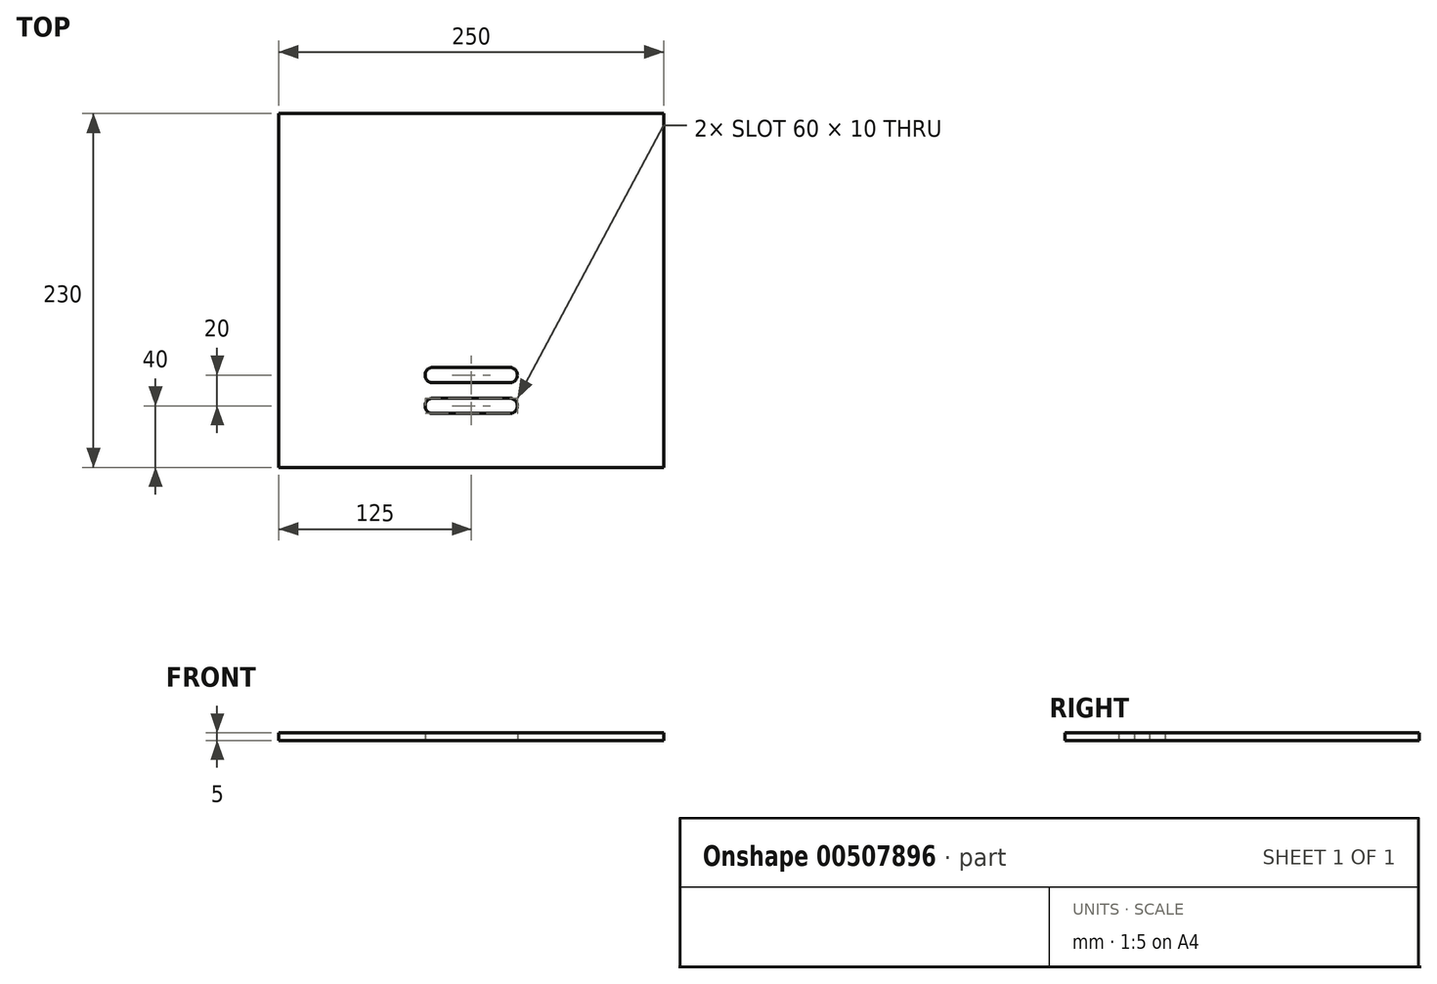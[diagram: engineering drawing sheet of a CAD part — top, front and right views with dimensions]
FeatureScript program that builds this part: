
annotation { "Feature Type Name" : "Feature", "Feature Type Description" : "" }
export const myFeature = defineFeature(function(context is Context, id is Id, definition is map)
    precondition{}
    {
        {
            var Q0;
            Q0=qCreatedBy(makeId("Top.planeOp"),FACE);
            var sketch = newSketch(context, id + "F0", { "sketchPlane" : qUnion([Q0])});
            skLineSegment(sketch, "E0.bottom", {"start": v(125, -115) * mm, "end": v(-125, -115) * mm});
            skLineSegment(sketch, "E0.top", {"start": v(125, 115) * mm, "end": v(-125, 115) * mm});
            skLineSegment(sketch, "E0.left", {"start": v(125, -115) * mm, "end": v(125, 115) * mm});
            skLineSegment(sketch, "E0.right", {"start": v(-125, -115) * mm, "end": v(-125, 115) * mm});
            skPoint(sketch, "E0.middle", {"position": v(0, 0) * mm});
            skLineSegment(sketch, "E1", {"start": v(0, -115) * mm, "end": v(0, 115) * mm, "construction": true});
            skLineSegment(sketch, "E2.1.0.0", {"start": v(25, -115) * mm, "end": v(25, 115) * mm, "construction": true});
            skLineSegment(sketch, "E2.2.0.0", {"start": v(50, -115) * mm, "end": v(50, 115) * mm, "construction": true});
            skLineSegment(sketch, "E2.3.0.0", {"start": v(75, -115) * mm, "end": v(75, 115) * mm, "construction": true});
            skLineSegment(sketch, "E2.4.0.0", {"start": v(100, -115) * mm, "end": v(100, 115) * mm, "construction": true});
            skLineSegment(sketch, "E2.direction1", {"start": v(0, -115) * mm, "end": v(25, -115) * mm, "construction": true});
            skLineSegment(sketch, "E3.1.0.0", {"start": v(-25, -115) * mm, "end": v(-25, 115) * mm, "construction": true});
            skLineSegment(sketch, "E3.2.0.0", {"start": v(-50, -115) * mm, "end": v(-50, 115) * mm, "construction": true});
            skLineSegment(sketch, "E3.3.0.0", {"start": v(-75, -115) * mm, "end": v(-75, 115) * mm, "construction": true});
            skLineSegment(sketch, "E3.4.0.0", {"start": v(-100, -115) * mm, "end": v(-100, 115) * mm, "construction": true});
            skLineSegment(sketch, "E3.direction1", {"start": v(0, -115) * mm, "end": v(-25, -115) * mm, "construction": true});
            skLineSegment(sketch, "E4", {"start": v(-125, 0) * mm, "end": v(125, 0) * mm, "construction": true});
            skLineSegment(sketch, "E5.0.1.0", {"start": v(-125, 25) * mm, "end": v(125, 25) * mm, "construction": true});
            skLineSegment(sketch, "E5.0.2.0", {"start": v(-125, 50) * mm, "end": v(125, 50) * mm, "construction": true});
            skLineSegment(sketch, "E5.0.3.0", {"start": v(-125, 75) * mm, "end": v(125, 75) * mm, "construction": true});
            skLineSegment(sketch, "E5.direction1", {"start": v(-125, 0) * mm, "end": v(-100, 0) * mm, "construction": true});
            skLineSegment(sketch, "E5.direction2", {"start": v(-125, 0) * mm, "end": v(-125, 25) * mm, "construction": true});
            skLineSegment(sketch, "E6.0.1.0", {"start": v(-125, -25) * mm, "end": v(125, -25) * mm, "construction": true});
            skLineSegment(sketch, "E6.0.2.0", {"start": v(-125, -50) * mm, "end": v(125, -50) * mm, "construction": true});
            skLineSegment(sketch, "E6.0.3.0", {"start": v(-125, -75) * mm, "end": v(125, -75) * mm, "construction": true});
            skLineSegment(sketch, "E6.direction2", {"start": v(-125, 0) * mm, "end": v(-125, -25) * mm, "construction": true});
            skLineSegment(sketch, "E7", {"start": v(0, -75) * mm, "end": v(0, -55) * mm, "construction": true});
            skLineSegment(sketch, "E8", {"start": v(25, -55) * mm, "end": v(-25, -55) * mm, "construction": true});
            skArc(sketch, "E9", {"start": v(-25, -50) * mm, "mid": v(-30, -55) * mm, "end": v(-25, -60) * mm});
            skArc(sketch, "E10", {"start": v(25, -50) * mm, "mid": v(30, -55) * mm, "end": v(25, -60) * mm});
            skArc(sketch, "E11", {"start": v(-25, -70) * mm, "mid": v(-30, -75) * mm, "end": v(-25, -80) * mm});
            skArc(sketch, "E12", {"start": v(25, -70) * mm, "mid": v(30, -75) * mm, "end": v(25, -80) * mm});
            skLineSegment(sketch, "E13", {"start": v(-25, -50) * mm, "end": v(25, -50) * mm});
            skLineSegment(sketch, "E14", {"start": v(-25, -60) * mm, "end": v(25, -60) * mm});
            skLineSegment(sketch, "E15", {"start": v(-25, -70) * mm, "end": v(25, -70) * mm});
            skLineSegment(sketch, "E16", {"start": v(25, -80) * mm, "end": v(-25, -80) * mm});
            skLineSegment(sketch, "E17", {"start": v(0, -75) * mm, "end": v(0, -65) * mm, "construction": true});
            skLineSegment(sketch, "E18", {"start": v(0, -65) * mm, "end": v(97, -65) * mm, "construction": true});
            skLineSegment(sketch, "E19", {"start": v(0, -65) * mm, "end": v(-95, -65) * mm, "construction": true});
            skLineSegment(sketch, "E20", {"start": v(97, -65) * mm, "end": v(97, -72.5) * mm, "construction": true});
            skLineSegment(sketch, "E21", {"start": v(97, -65) * mm, "end": v(97, -55) * mm, "construction": true});
            skLineSegment(sketch, "E22", {"start": v(97, -55) * mm, "end": v(117, -55) * mm, "construction": true});
            skLineSegment(sketch, "E23", {"start": v(117, -55) * mm, "end": v(117, -56) * mm, "construction": true});
            skLineSegment(sketch, "E24", {"start": v(125, -50) * mm, "end": v(125, -45) * mm, "construction": true});
            skLineSegment(sketch, "E25", {"start": v(0, -55) * mm, "end": v(-95, -55) * mm, "construction": true});
            skPoint(sketch, "E25.endSnap0", {"position": v(-30, -55) * mm});
            skLineSegment(sketch, "E26", {"start": v(0, -65) * mm, "end": v(30, -65) * mm, "construction": true});
            skSolve(sketch);
        }
        {
            var Q0;
            Q0=makeQuery(id+"F0.imprint","IMPRINT",FACE,{"disambiguationData":[TD([[makeQuery(id+"F0.imprint","IMPRINT",EDGE,{"derivedFrom":sQuery(id+"F0.wireOp",EDGE,"E0.bottom")}),-1.0]])]});
            extrude(context, id + "F1", {"entities" : qUnion([Q0]), "depth" : 5 * mm, "offsetDistance" : 25 * mm});
        }
    });
